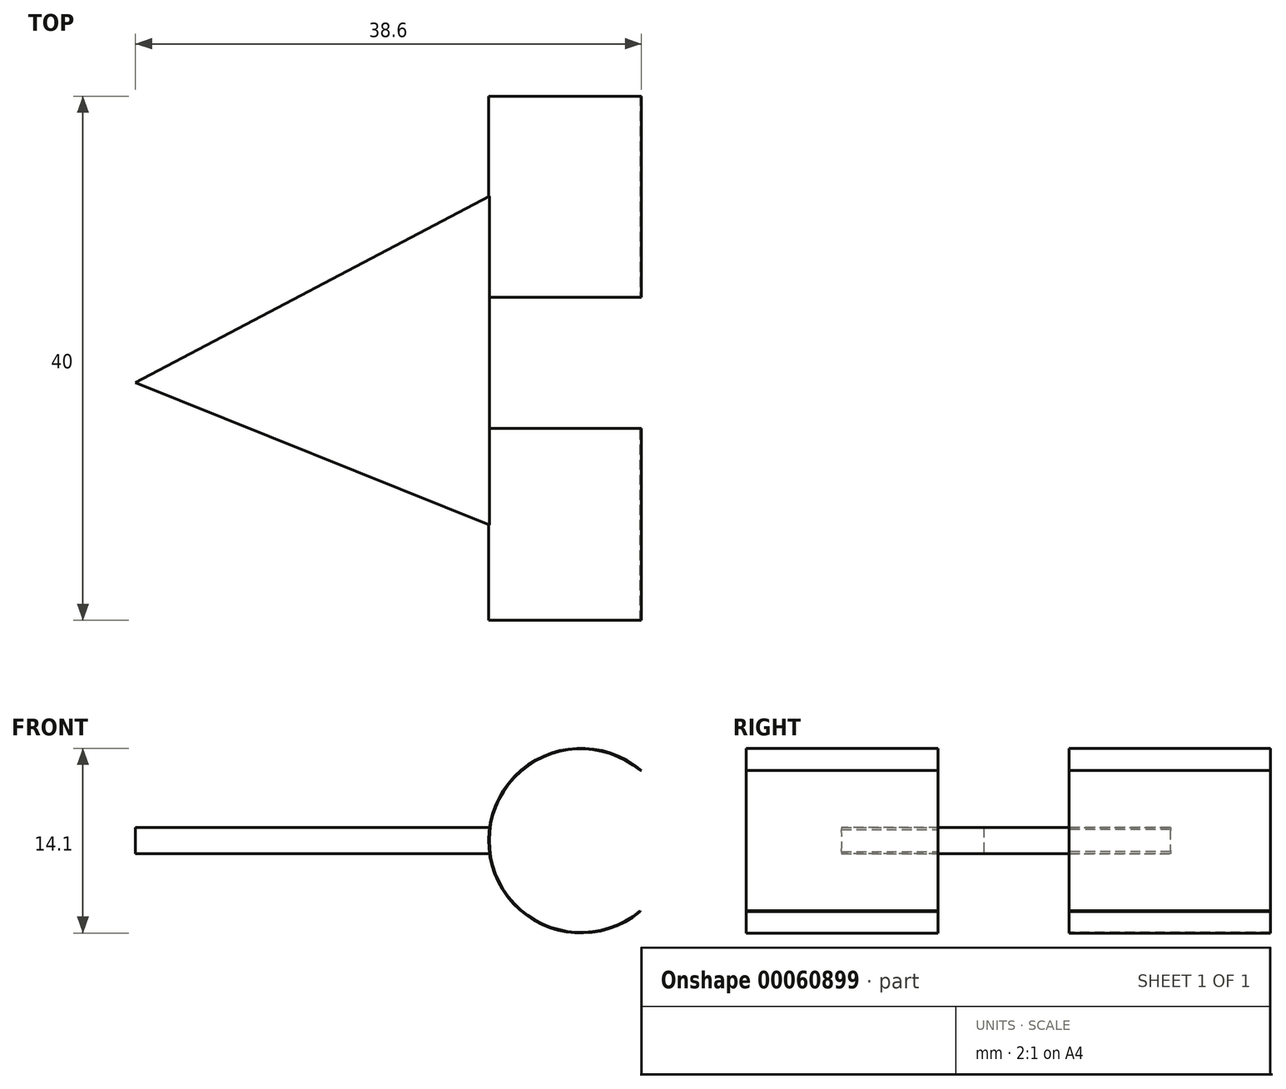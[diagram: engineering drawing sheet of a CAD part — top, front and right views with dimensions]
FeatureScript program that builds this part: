
annotation { "Feature Type Name" : "Feature", "Feature Type Description" : "" }
export const myFeature = defineFeature(function(context is Context, id is Id, definition is map)
    precondition{}
    {
        {
            var Q0;
            Q0=qCreatedBy(makeId("Front.planeOp"),FACE);
            cPlane(context, id + "F0", {"entities" : qUnion([Q0]), "cplaneType" : CPlaneType.OFFSET, "offset" : 4.64 * mm, "oppositeDirection" : true, "width" : 150 * mm, "height" : 150 * mm});
        }
        {
            var Q0;
            Q0=qCreatedBy(id+"F0.planeOp",FACE);
            var sketch = newSketch(context, id + "F1", { "sketchPlane" : qUnion([Q0])});
            skCircle(sketch, "E0", {"center": v(34, 17.05) * mm, "radius": 7.05 * mm});
            skCircle(sketch, "E1", {"center": v(34, 17.05) * mm, "radius": 7 * mm});
            skSolve(sketch);
        }
        {
            var Q0;
            Q0=makeQuery(id+"F1.imprint","IMPRINT",FACE,{"disambiguationData":[TD([[makeQuery(id+"F1.imprint","IMPRINT",EDGE,{"derivedFrom":sQuery(id+"F1.wireOp",EDGE,"E0")}),1.0]])]});
            var Q1;
            Q1=sQuery(id+"F1.wireOp",EDGE,"E0");
            extrude(context, id + "F2", {"entities" : qUnion([Q0]), "surfaceEntities" : qUnion([Q1]), "oppositeDirection" : true, "depth" : 15.36 * mm});
        }
        {
            var Q0;
            Q0=qCreatedBy(makeId("Front.planeOp"),FACE);
            cPlane(context, id + "F3", {"entities" : qUnion([Q0]), "cplaneType" : CPlaneType.OFFSET, "offset" : 5.36 * mm, "width" : 150 * mm, "height" : 150 * mm});
        }
        {
            var Q0;
            Q0=qCreatedBy(id+"F3.planeOp",FACE);
            var sketch = newSketch(context, id + "F4", { "sketchPlane" : qUnion([Q0])});
            skCircle(sketch, "E2", {"center": v(34, 17.05) * mm, "radius": 7.05 * mm});
            skCircle(sketch, "E3", {"center": v(34, 17.05) * mm, "radius": 7 * mm});
            skSolve(sketch);
        }
        {
            var Q0;
            Q0=makeQuery(id+"F4.imprint","IMPRINT",FACE,{"disambiguationData":[TD([[makeQuery(id+"F4.imprint","IMPRINT",EDGE,{"derivedFrom":sQuery(id+"F4.wireOp",EDGE,"E2")}),1.0]])]});
            var Q1;
            Q1=sQuery(id+"F4.wireOp",EDGE,"E2");
            extrude(context, id + "F5", {"entities" : qUnion([Q0]), "surfaceEntities" : qUnion([Q1]), "depth" : 14.64 * mm});
        }
        {
            var Q0;
            Q0=qCreatedBy(makeId("Top.planeOp"),FACE);
            cPlane(context, id + "F6", {"entities" : qUnion([Q0]), "cplaneType" : CPlaneType.OFFSET, "offset" : 17.05 * mm, "width" : 150 * mm, "height" : 150 * mm});
        }
        {
            var Q0;
            Q0=qCreatedBy(id+"F6.planeOp",FACE);
            var sketch = newSketch(context, id + "F7", { "sketchPlane" : qUnion([Q0])});
            skLineSegment(sketch, "E4", {"start": v(27, 12.38) * mm, "end": v(0, -1.86) * mm});
            skLineSegment(sketch, "E5", {"start": v(0, -1.86) * mm, "end": v(27, -12.72) * mm});
            skLineSegment(sketch, "E6", {"start": v(27, -12.72) * mm, "end": v(27, 12.38) * mm});
            skSolve(sketch);
        }
        {
            var Q0;
            Q0=makeQuery(id+"F7.imprint","IMPRINT",FACE,{"disambiguationData":[TD([[makeQuery(id+"F7.imprint","IMPRINT",EDGE,{"derivedFrom":sQuery(id+"F7.wireOp",EDGE,"E4")}),1.0]])]});
            extrude(context, id + "F8", {"entities" : qUnion([Q0]), "operationType" : NewBodyOperationType.ADD, "endBound" : BoundingType.SYMMETRIC, "depth" : 2 * mm});
        }
        {
            var Q0;
            Q0=qCreatedBy(makeId("Right.planeOp"),FACE);
            cPlane(context, id + "F9", {"entities" : qUnion([Q0]), "cplaneType" : CPlaneType.OFFSET, "offset" : 38.5 * mm, "width" : 150 * mm, "height" : 150 * mm});
        }
        {
            var Q0;
            Q0=qCreatedBy(id+"F9.planeOp",FACE);
            var sketch = newSketch(context, id + "F10", { "sketchPlane" : qUnion([Q0])});
            skLineSegment(sketch, "E7.bottom", {"start": v(-20.7, 22.4) * mm, "end": v(22.67, 22.4) * mm});
            skLineSegment(sketch, "E7.top", {"start": v(-20.7, 11.62) * mm, "end": v(22.67, 11.62) * mm});
            skLineSegment(sketch, "E7.left", {"start": v(-20.7, 22.4) * mm, "end": v(-20.7, 11.62) * mm});
            skLineSegment(sketch, "E7.right", {"start": v(22.67, 22.4) * mm, "end": v(22.67, 11.62) * mm});
            skSolve(sketch);
        }
        {
            var Q0;
            Q0 = qSketchRegion(id + "F10", true);
            extrude(context, id + "F11", {"entities" : qUnion([Q0]), "operationType" : NewBodyOperationType.REMOVE, "depth" : 25 * mm});
        }
    });
